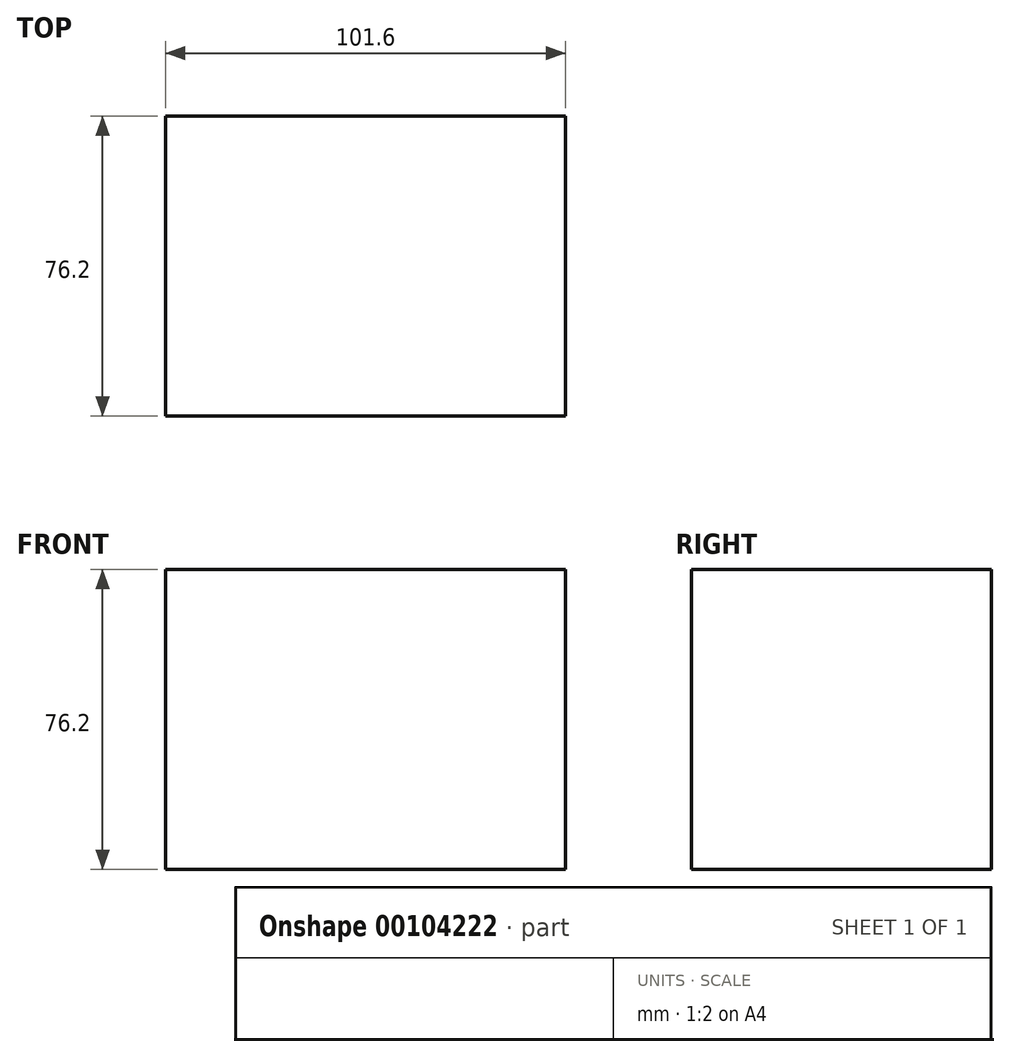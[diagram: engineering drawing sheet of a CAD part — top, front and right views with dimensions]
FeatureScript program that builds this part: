
annotation { "Feature Type Name" : "Feature", "Feature Type Description" : "" }
export const myFeature = defineFeature(function(context is Context, id is Id, definition is map)
    precondition{}
    {
        {
            var Q0;
            Q0=qCreatedBy(makeId("Front.planeOp"),FACE);
            var sketch = newSketch(context, id + "F0", { "sketchPlane" : qUnion([Q0])});
            skLineSegment(sketch, "E0.bottom", {"start": v(-50.8, 38.1) * mm, "end": v(50.8, 38.1) * mm});
            skLineSegment(sketch, "E0.top", {"start": v(-50.8, -38.1) * mm, "end": v(50.8, -38.1) * mm});
            skLineSegment(sketch, "E0.left", {"start": v(-50.8, 38.1) * mm, "end": v(-50.8, -38.1) * mm});
            skLineSegment(sketch, "E0.right", {"start": v(50.8, 38.1) * mm, "end": v(50.8, -38.1) * mm});
            skPoint(sketch, "E0.middle", {"position": v(0, 0) * mm});
            skSolve(sketch);
        }
        {
            var Q0;
            Q0=makeQuery(id+"F0.imprint","IMPRINT",FACE,{"disambiguationData":[TD([[makeQuery(id+"F0.imprint","IMPRINT",EDGE,{"derivedFrom":sQuery(id+"F0.wireOp",EDGE,"E0.bottom")}),-1.0]])]});
            extrude(context, id + "F1", {"entities" : qUnion([Q0]), "endBound" : BoundingType.SYMMETRIC, "depth" : 76.2 * mm});
        }
    });
